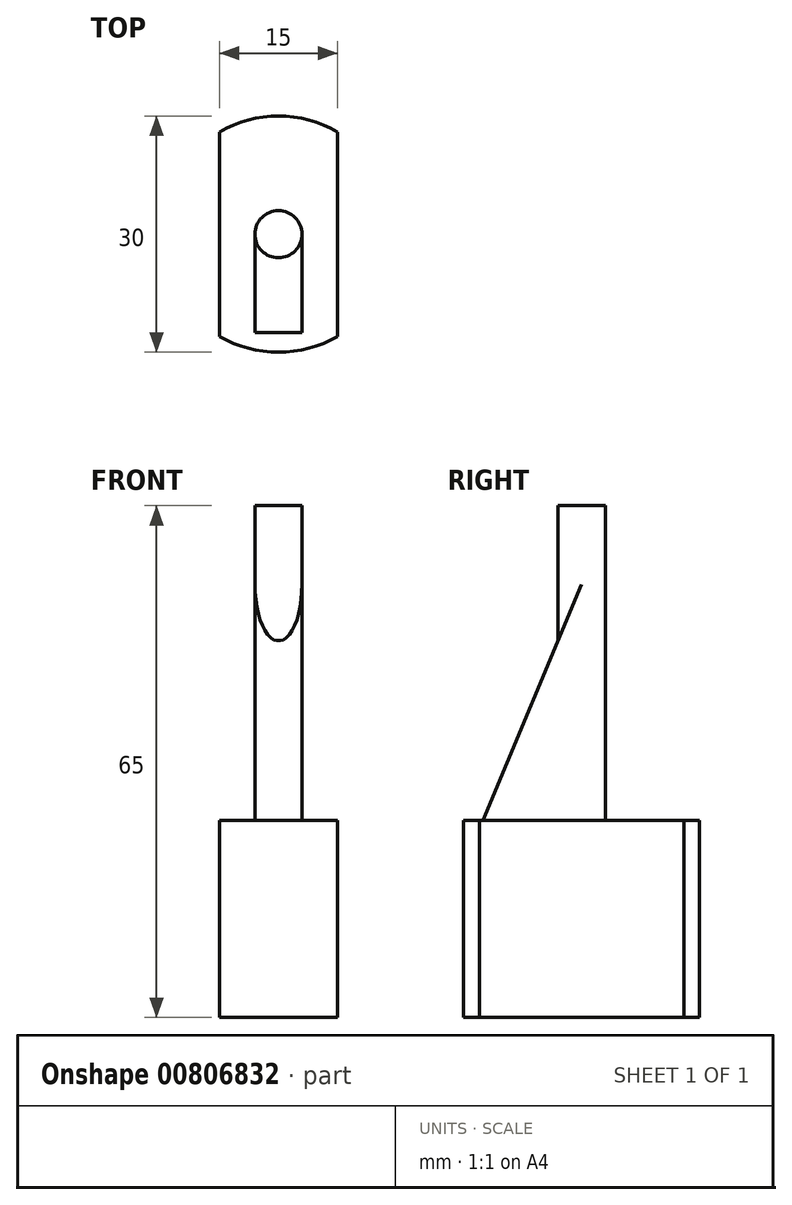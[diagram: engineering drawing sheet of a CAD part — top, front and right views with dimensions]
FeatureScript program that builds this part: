
annotation { "Feature Type Name" : "Feature", "Feature Type Description" : "" }
export const myFeature = defineFeature(function(context is Context, id is Id, definition is map)
    precondition{}
    {
        {
            var Q0;
            Q0=qCreatedBy(makeId("Top.planeOp"),FACE);
            var sketch = newSketch(context, id + "F0", { "sketchPlane" : qUnion([Q0])});
            skCircle(sketch, "E0", {"center": v(0, 0) * mm, "radius": 15 * mm});
            skCircle(sketch, "E1", {"center": v(0, 0) * mm, "radius": 3 * mm});
            skLineSegment(sketch, "E2.bottom", {"start": v(7.5, 20) * mm, "end": v(-7.5, 20) * mm});
            skLineSegment(sketch, "E2.top", {"start": v(7.5, -20) * mm, "end": v(-7.5, -20) * mm});
            skLineSegment(sketch, "E2.left", {"start": v(7.5, 20) * mm, "end": v(7.5, -20) * mm});
            skLineSegment(sketch, "E2.right", {"start": v(-7.5, 20) * mm, "end": v(-7.5, -20) * mm});
            skSolve(sketch);
        }
        {
            var Q0;
            Q0=makeQuery(id+"F0.imprint","IMPRINT",FACE,{"disambiguationData":[TD([[makeQuery(id+"F0.imprint","IMPRINT",EDGE,{"derivedFrom":sQuery(id+"F0.wireOp",EDGE,"E1")}),-1.0]])]});
            extrude(context, id + "F1", {"entities" : qUnion([Q0]), "depth" : 25 * mm, "offsetDistance" : 25 * mm});
        }
        {
            var Q0;
            Q0=makeQuery(id+"F0.imprint","IMPRINT",FACE,{"disambiguationData":[TD([[makeQuery(id+"F0.imprint","IMPRINT",EDGE,{"derivedFrom":sQuery(id+"F0.wireOp",EDGE,"E1")}),1.0]])]});
            extrude(context, id + "F2", {"entities" : qUnion([Q0]), "operationType" : NewBodyOperationType.ADD, "depth" : 65 * mm, "offsetDistance" : 25 * mm});
        }
        {
            var Q0;
            Q0=qCreatedBy(makeId("Right.planeOp"),FACE);
            var sketch = newSketch(context, id + "F3", { "sketchPlane" : qUnion([Q0])});
            skLineSegment(sketch, "E3", {"start": v(0, 0) * mm, "end": v(0, 25) * mm});
            skLineSegment(sketch, "E4", {"start": v(0, 25) * mm, "end": v(0, 55) * mm});
            skLineSegment(sketch, "E5", {"start": v(0, 55) * mm, "end": v(-12.5, 25) * mm});
            skLineSegment(sketch, "E6", {"start": v(-12.5, 25) * mm, "end": v(0, 25) * mm});
            skSolve(sketch);
        }
        {
            var Q0;
            Q0 = qSketchRegion(id + "F3", true);
            extrude(context, id + "F4", {"entities" : qUnion([Q0]), "operationType" : NewBodyOperationType.ADD, "endBound" : BoundingType.SYMMETRIC, "depth" : 6 * mm, "offsetDistance" : 25 * mm});
        }
    });
